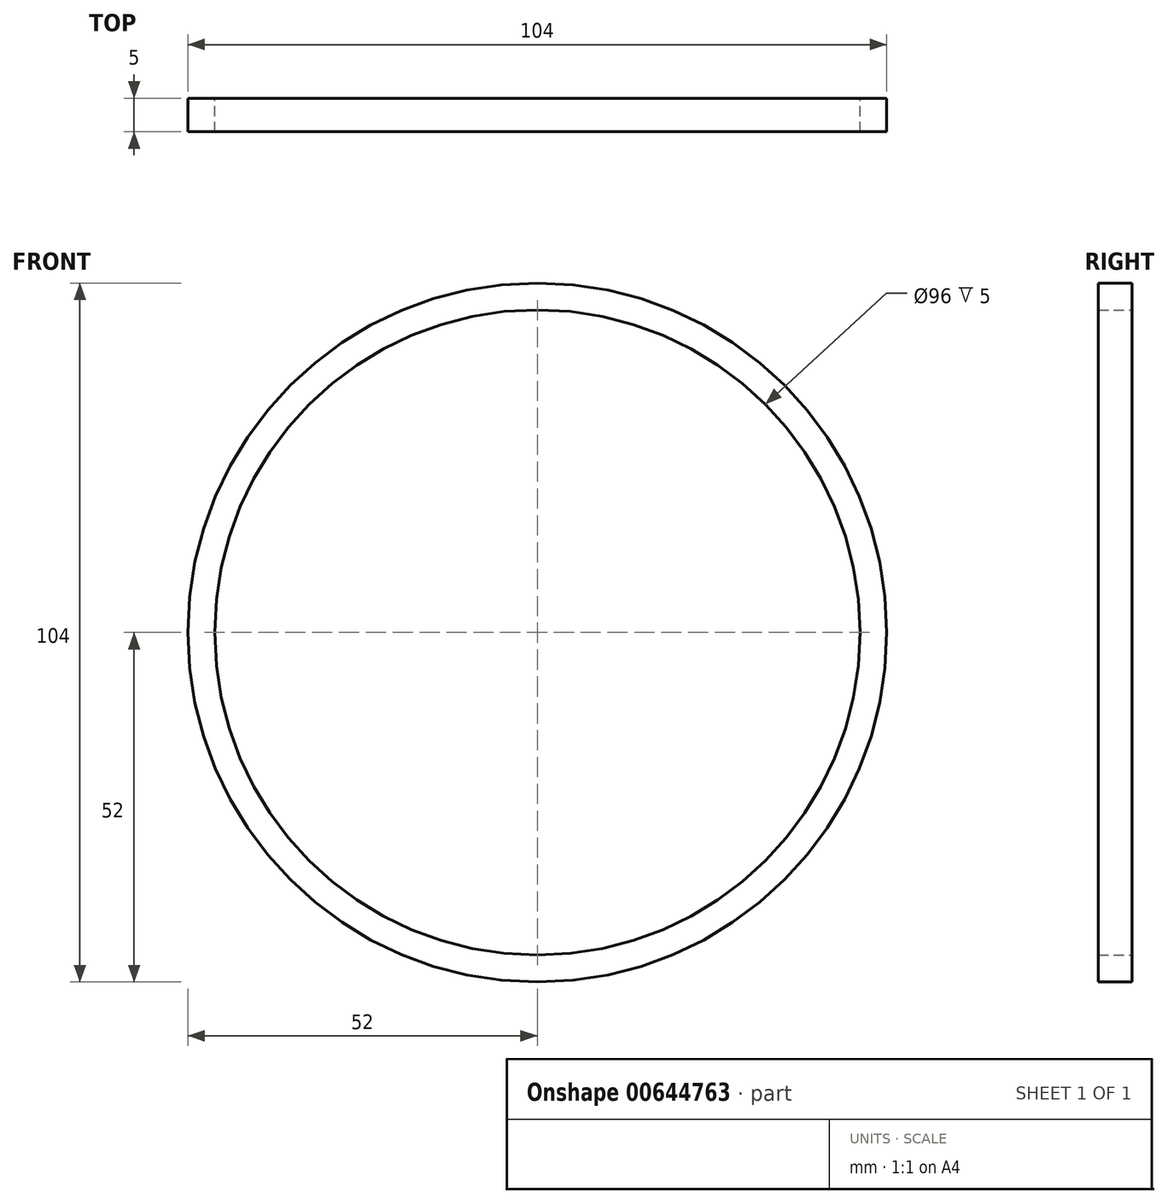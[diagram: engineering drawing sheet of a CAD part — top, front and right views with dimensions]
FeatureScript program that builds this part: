
annotation { "Feature Type Name" : "Feature", "Feature Type Description" : "" }
export const myFeature = defineFeature(function(context is Context, id is Id, definition is map)
    precondition{}
    {
        {
            var Q0;
            Q0=qCreatedBy(makeId("Front.planeOp"),FACE);
            var sketch = newSketch(context, id + "F0", { "sketchPlane" : qUnion([Q0])});
            skCircle(sketch, "E0", {"center": v(0, 0) * mm, "radius": 52 * mm});
            skCircle(sketch, "E1", {"center": v(0, 0) * mm, "radius": 48 * mm});
            skSolve(sketch);
        }
        {
            var Q0;
            Q0=makeQuery(id+"F0.imprint","IMPRINT",FACE,{"disambiguationData":[TD([[makeQuery(id+"F0.imprint","IMPRINT",EDGE,{"derivedFrom":sQuery(id+"F0.wireOp",EDGE,"E0")}),1.0]])]});
            extrude(context, id + "F1", {"entities" : qUnion([Q0]), "depth" : 5 * mm, "offsetDistance" : 25 * mm});
        }
    });
